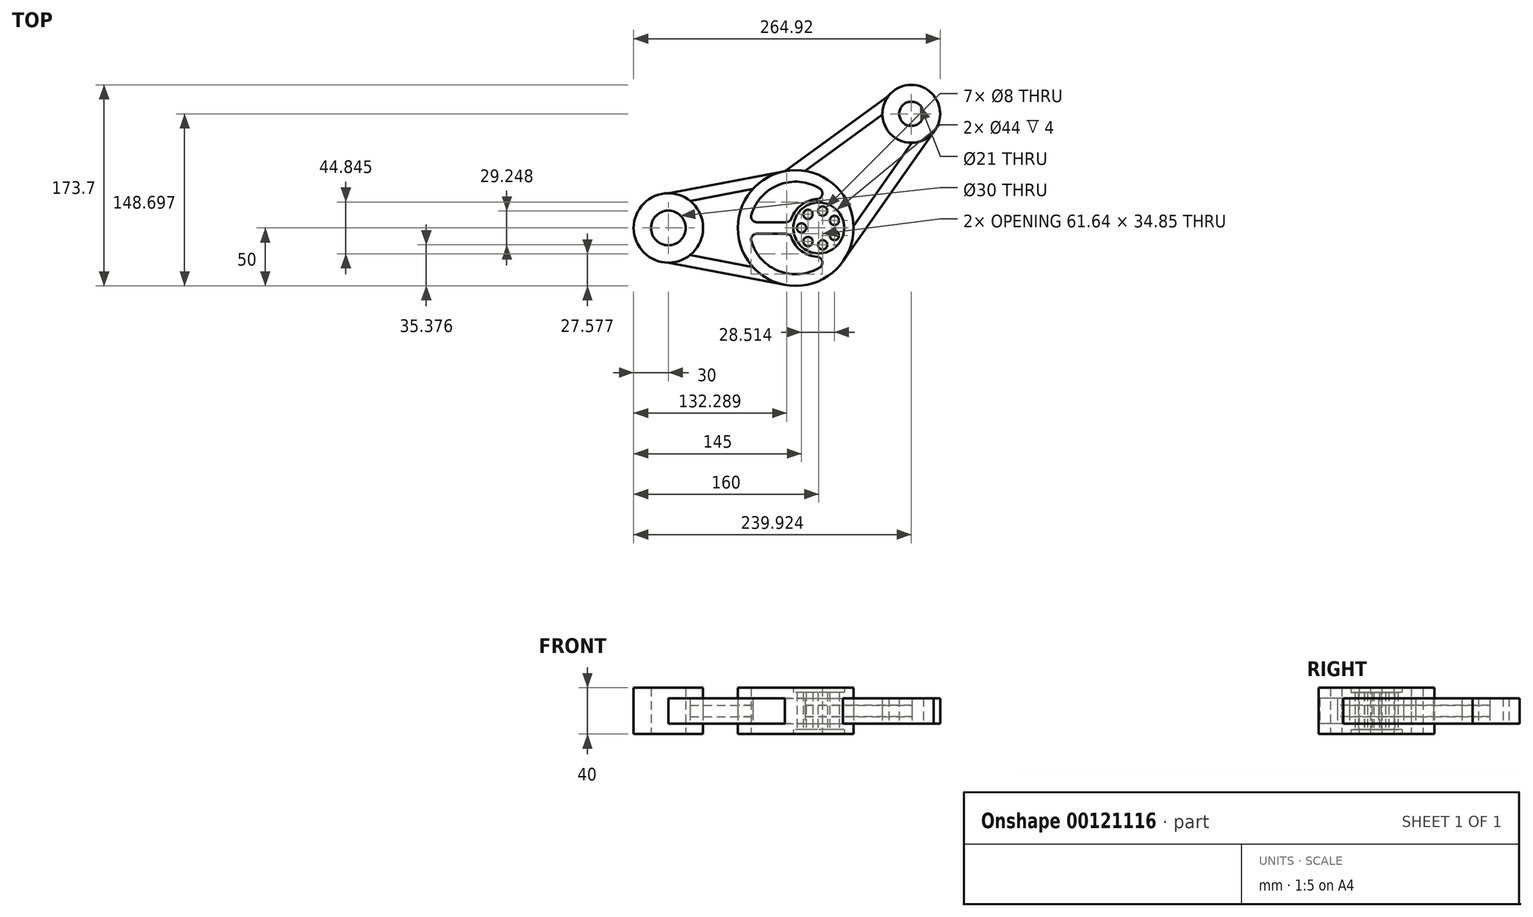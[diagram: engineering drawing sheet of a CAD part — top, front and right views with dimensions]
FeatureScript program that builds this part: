
annotation { "Feature Type Name" : "Feature", "Feature Type Description" : "" }
export const myFeature = defineFeature(function(context is Context, id is Id, definition is map)
    precondition{}
    {
        {
            var Q0;
            Q0=qCreatedBy(makeId("Top.planeOp"),FACE);
            var sketch = newSketch(context, id + "F0", { "sketchPlane" : qUnion([Q0])});
            skCircle(sketch, "E0", {"center": v(0, 0) * mm, "radius": 22 * mm});
            skCircle(sketch, "E1", {"center": v(-130, 0) * mm, "radius": 30 * mm});
            skCircle(sketch, "E2", {"center": v(79.92, 98.7) * mm, "radius": 25 * mm});
            skCircle(sketch, "E3", {"center": v(-20, 0) * mm, "radius": 50 * mm});
            skLineSegment(sketch, "E4.0", {"start": v(-24.5, 5) * mm, "end": v(-59.69, 5) * mm});
            skLineSegment(sketch, "E5.0", {"start": v(-24.5, -5) * mm, "end": v(-59.69, -5) * mm});
            skArc(sketch, "E6", {"start": v(14.37, 20.45) * mm, "mid": v(-9.24, 23.23) * mm, "end": v(-24.5, 5) * mm});
            skArc(sketch, "E7.0", {"start": v(14.37, 20.45) * mm, "mid": v(-28.17, 39.16) * mm, "end": v(-59.69, 5) * mm});
            skArc(sketch, "E8.trimOffspring", {"start": v(-24.5, -5) * mm, "mid": v(-9.24, -23.23) * mm, "end": v(14.37, -20.45) * mm});
            skArc(sketch, "E9.trimOffspring", {"start": v(-59.69, -5) * mm, "mid": v(-28.17, -39.16) * mm, "end": v(14.37, -20.45) * mm});
            skLineSegment(sketch, "E10", {"start": v(-130, 30) * mm, "end": v(-29.33, 49.12) * mm});
            skLineSegment(sketch, "E11.MirrorCS", {"start": v(-130, -30) * mm, "end": v(-29.33, -49.12) * mm});
            skCircle(sketch, "E12", {"center": v(-130, 0) * mm, "radius": 15 * mm});
            skLineSegment(sketch, "E13", {"start": v(-29.33, 49.12) * mm, "end": v(60.5, 114.43) * mm});
            skLineSegment(sketch, "E14", {"start": v(99.35, 82.96) * mm, "end": v(20.92, -28.73) * mm});
            skCircle(sketch, "E15", {"center": v(79.92, 98.7) * mm, "radius": 10.5 * mm});
            skLineSegment(sketch, "E16.0", {"start": v(80.63, 73.7) * mm, "end": v(29.98, 1.57) * mm});
            skLineSegment(sketch, "E17.0", {"start": v(-111.21, 23.39) * mm, "end": v(-56.94, 33.7) * mm});
            skLineSegment(sketch, "E18.0", {"start": v(-111.21, -23.39) * mm, "end": v(-56.94, -33.7) * mm});
            skCircle(sketch, "E19", {"center": v(-15, 0) * mm, "radius": 4 * mm});
            skCircle(sketch, "E20.1.0", {"center": v(-9.35, -11.73) * mm, "radius": 4 * mm});
            skCircle(sketch, "E20.2.0", {"center": v(3.34, -14.62) * mm, "radius": 4 * mm});
            skCircle(sketch, "E21.1.3.0", {"center": v(13.51, -6.5) * mm, "radius": 4 * mm});
            skCircle(sketch, "E21.1.4.0", {"center": v(13.51, 6.5) * mm, "radius": 4 * mm});
            skCircle(sketch, "E21.1.5.0", {"center": v(3.34, 14.62) * mm, "radius": 4 * mm});
            skCircle(sketch, "E21.1.6.0", {"center": v(-9.35, 11.73) * mm, "radius": 4 * mm});
            skLineSegment(sketch, "E22.0", {"start": v(-12, 49.36) * mm, "end": v(54.93, 98.02) * mm});
            skSolve(sketch);
        }
        {
            var Q0;
            Q0=makeQuery(id+"F0.imprint","IMPRINT",FACE,{"disambiguationData":[TD([[makeQuery(id+"F0.imprint","IMPRINT",EDGE,{"derivedFrom":sQuery(id+"F0.wireOp",EDGE,"E12")}),-1.0]])]});
            var Q1;
            Q1=makeQuery(id+"F0.imprint","IMPRINT",FACE,{"disambiguationData":[TD([[makeQuery(id+"F0.imprint","IMPRINT",EDGE,{"derivedFrom":sQuery(id+"F0.wireOp",EDGE,"E0")}),-1.0]])]});
            extrude(context, id + "F1", {"entities" : qUnion([Q0, Q1]), "depth" : 40 * mm, "symmetric" : true});
        }
        {
            var Q0;
            {var subQ0=sQuery(id+"F0.wireOp",EDGE,"E10");Q0=makeQuery(id+"F0.imprint","IMPRINT",FACE,{"disambiguationData":[TD([[makeQuery(id+"F0.imprint","IMPRINT",EDGE,{"derivedFrom":subQ0}),-1.0]])]});}
            var Q1;
            {var subQ0=sQuery(id+"F0.wireOp",EDGE,"E11.MirrorCS");Q1=makeQuery(id+"F0.imprint","IMPRINT",FACE,{"disambiguationData":[TD([[makeQuery(id+"F0.imprint","IMPRINT",EDGE,{"derivedFrom":subQ0}),1.0]])]});}
            var Q2;
            {var subQ0=sQuery(id+"F0.wireOp",EDGE,"E14");Q2=makeQuery(id+"F0.imprint","IMPRINT",FACE,{"disambiguationData":[TD([[makeQuery(id+"F0.imprint","IMPRINT",EDGE,{"derivedFrom":subQ0}),-1.0]])]});}
            var Q3;
            {var subQ0=sQuery(id+"F0.wireOp",EDGE,"E13");Q3=makeQuery(id+"F0.imprint","IMPRINT",FACE,{"disambiguationData":[TD([[makeQuery(id+"F0.imprint","IMPRINT",EDGE,{"derivedFrom":subQ0}),-1.0]])]});}
            extrude(context, id + "F2", {"entities" : qUnion([Q0, Q1, Q2, Q3]), "depth" : 22 * mm, "symmetric" : true});
        }
        {
            var Q0;
            Q0=makeQuery(id+"F0.imprint","IMPRINT",FACE,{"disambiguationData":[TD([[makeQuery(id+"F0.imprint","IMPRINT",EDGE,{"derivedFrom":sQuery(id+"F0.wireOp",EDGE,"E15")}),-1.0]])]});
            extrude(context, id + "F3", {"entities" : qUnion([Q0]), "depth" : 22 * mm, "symmetric" : true});
        }
        {
            var Q0;
            Q0=makeQuery(id+"F0.imprint","IMPRINT",FACE,{"disambiguationData":[TD([[makeQuery(id+"F0.imprint","IMPRINT",EDGE,{"derivedFrom":sQuery(id+"F0.wireOp",EDGE,"E0")}),1.0]])]});
            extrude(context, id + "F4", {"entities" : qUnion([Q0]), "operationType" : NewBodyOperationType.ADD, "depth" : 32 * mm, "symmetric" : true});
        }
        {
            var Q0;
            {var subQ0=sQuery(id+"F0.wireOp",EDGE,"E16.0");Q0=makeQuery(id+"F0.imprint","IMPRINT",FACE,{"disambiguationData":[TD([[makeQuery(id+"F0.imprint","IMPRINT",EDGE,{"derivedFrom":subQ0}),-1.0]])]});}
            var Q1;
            {var subQ0=sQuery(id+"F0.wireOp",EDGE,"E17.0");Q1=makeQuery(id+"F0.imprint","IMPRINT",FACE,{"disambiguationData":[TD([[makeQuery(id+"F0.imprint","IMPRINT",EDGE,{"derivedFrom":subQ0}),-1.0]])]});}
            extrude(context, id + "F5", {"entities" : qUnion([Q0, Q1]), "depth" : 10 * mm, "symmetric" : true});
        }
        {
            var Q0;
            Q0=makeQuery(id+"F1.opExtrude","SWEPT_EDGE",EDGE,{"disambiguationData":[OSD([sQuery(id+"F0.wireOp",EDGE,"E4.0"),sQuery(id+"F0.wireOp",EDGE,"E7.0")])]});
            var Q1;
            Q1=makeQuery(id+"F1.opExtrude","SWEPT_EDGE",EDGE,{"disambiguationData":[OSD([sQuery(id+"F0.wireOp",EDGE,"E5.0"),sQuery(id+"F0.wireOp",EDGE,"E8.trimOffspring")])]});
            var Q2;
            Q2=makeQuery(id+"F1.opExtrude","SWEPT_EDGE",EDGE,{"disambiguationData":[OSD([sQuery(id+"F0.wireOp",EDGE,"E8.trimOffspring"),sQuery(id+"F0.wireOp",EDGE,"E9.trimOffspring")])]});
            var Q3;
            Q3=makeQuery(id+"F1.opExtrude","SWEPT_EDGE",EDGE,{"disambiguationData":[OSD([sQuery(id+"F0.wireOp",EDGE,"E5.0"),sQuery(id+"F0.wireOp",EDGE,"E9.trimOffspring")])]});
            var Q4;
            Q4=makeQuery(id+"F1.opExtrude","SWEPT_EDGE",EDGE,{"disambiguationData":[OSD([sQuery(id+"F0.wireOp",EDGE,"E6"),sQuery(id+"F0.wireOp",EDGE,"E7.0")])]});
            var Q5;
            Q5=makeQuery(id+"F1.opExtrude","SWEPT_EDGE",EDGE,{"disambiguationData":[OSD([sQuery(id+"F0.wireOp",EDGE,"E4.0"),sQuery(id+"F0.wireOp",EDGE,"E6")])]});
            fillet(context, id + "F6", {"entities" : qUnion([Q0, Q1, Q2, Q3, Q4, Q5]), "radius" : 5 * mm, "tangentPropagation" : true, "allowEdgeOverflow" : false});
        }
    });
